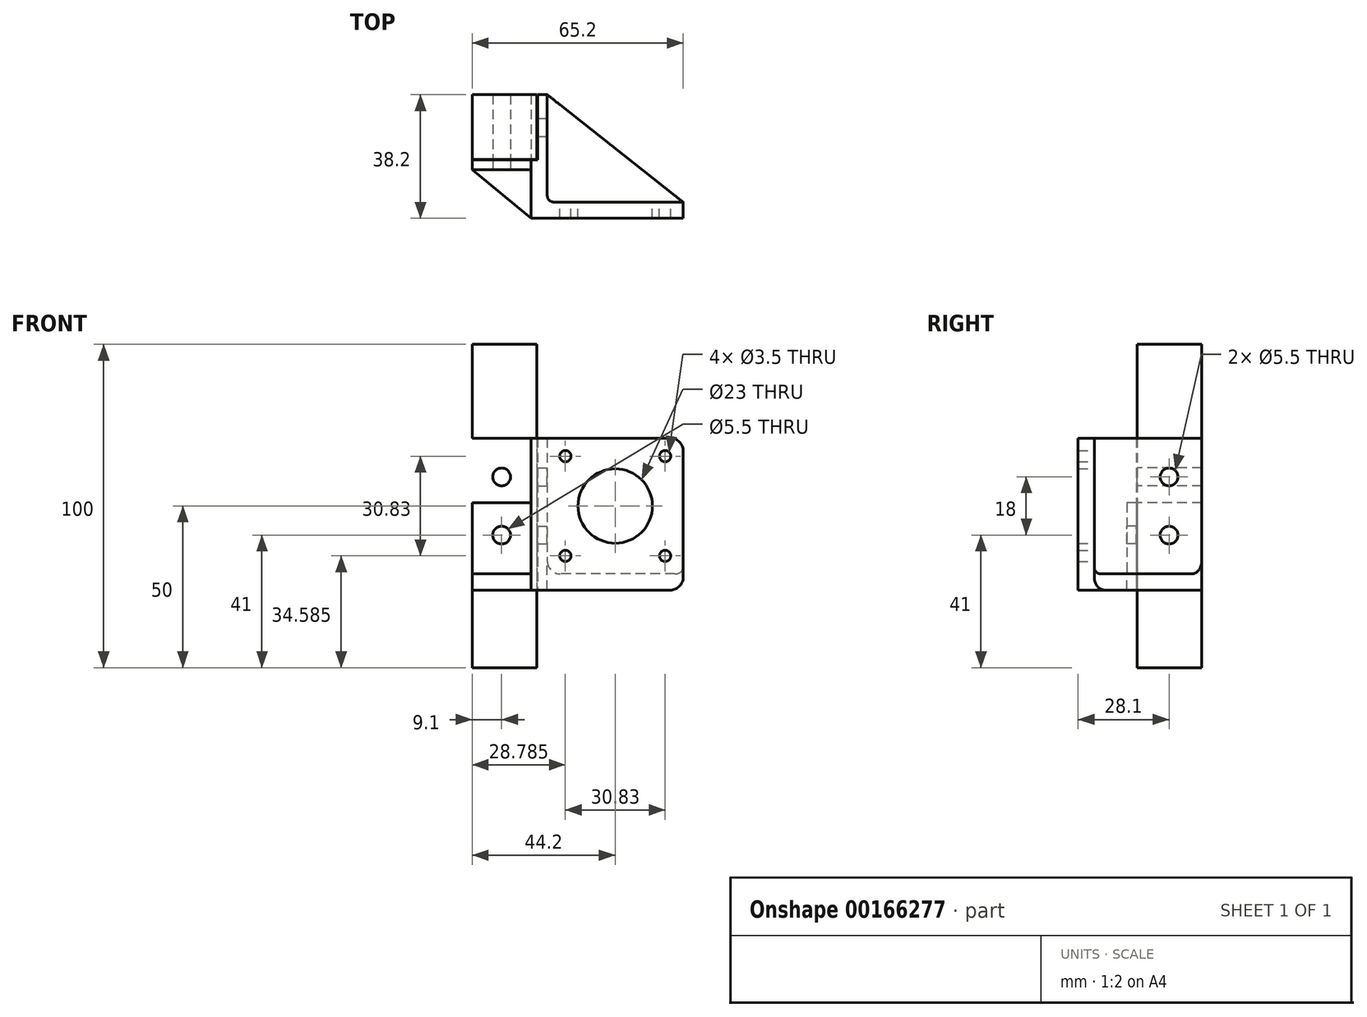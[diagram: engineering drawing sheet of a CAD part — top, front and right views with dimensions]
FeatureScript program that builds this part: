
annotation { "Feature Type Name" : "Feature", "Feature Type Description" : "" }
export const myFeature = defineFeature(function(context is Context, id is Id, definition is map)
    precondition{}
    {
        {
            var Q0;
            Q0=qCreatedBy(makeId("Top.planeOp"),FACE);
            var sketch = newSketch(context, id + "F0", { "sketchPlane" : qUnion([Q0])});
            skLineSegment(sketch, "E0.bottom", {"start": v(10, 10) * mm, "end": v(-10, 10) * mm});
            skLineSegment(sketch, "E0.top", {"start": v(10, -10) * mm, "end": v(-10, -10) * mm});
            skLineSegment(sketch, "E0.left", {"start": v(10, 10) * mm, "end": v(10, -10) * mm});
            skLineSegment(sketch, "E0.right", {"start": v(-10, 10) * mm, "end": v(-10, -10) * mm});
            skPoint(sketch, "E0.middle", {"position": v(0, 0) * mm});
            skSolve(sketch);
        }
        {
            var Q0;
            Q0 = qSketchRegion(id + "F0", true);
            extrude(context, id + "F1", {"entities" : qUnion([Q0]), "endBound" : BoundingType.SYMMETRIC, "depth" : 100 * mm});
        }
        {
            var Q0;
            Q0=qCreatedBy(makeId("Top.planeOp"),FACE);
            var sketch = newSketch(context, id + "F2", { "sketchPlane" : qUnion([Q0])});
            skLineSegment(sketch, "E1.0", {"start": v(10, 10) * mm, "end": v(10, -10) * mm, "construction": true});
            skLineSegment(sketch, "E2.0", {"start": v(10, -10) * mm, "end": v(-10, -10) * mm, "construction": true});
            skLineSegment(sketch, "E3.0", {"start": v(10.2, -10.2) * mm, "end": v(-10, -10.2) * mm});
            skLineSegment(sketch, "E4.0", {"start": v(10.2, 10) * mm, "end": v(10.2, -10.2) * mm});
            skLineSegment(sketch, "E5", {"start": v(10.2, 10) * mm, "end": v(13.2, 10) * mm});
            skLineSegment(sketch, "E6", {"start": v(13.2, 10) * mm, "end": v(13.2, -23.2) * mm});
            skLineSegment(sketch, "E7", {"start": v(-10, -10.2) * mm, "end": v(-10, -13.2) * mm});
            skLineSegment(sketch, "E8", {"start": v(8.2, -28.2) * mm, "end": v(55.2, -28.2) * mm});
            skLineSegment(sketch, "E9", {"start": v(55.2, -28.2) * mm, "end": v(55.2, -23.2) * mm});
            skLineSegment(sketch, "E10", {"start": v(55.2, -23.2) * mm, "end": v(13.2, -23.2) * mm});
            skLineSegment(sketch, "E11", {"start": v(-10, -13.2) * mm, "end": v(8.2, -13.2) * mm});
            skLineSegment(sketch, "E12", {"start": v(8.2, -13.2) * mm, "end": v(8.2, -28.2) * mm});
            skPoint(sketch, "E13.orphan", {"position": v(10.2, -13.2) * mm});
            skSolve(sketch);
        }
        {
            var Q0;
            Q0=makeQuery(id+"F2.imprint","IMPRINT",FACE,{"disambiguationData":[TD([[makeQuery(id+"F2.imprint","IMPRINT",EDGE,{"derivedFrom":sQuery(id+"F2.wireOp",EDGE,"E3.0")}),1.0]])]});
            extrude(context, id + "F3", {"entities" : qUnion([Q0]), "endBound" : BoundingType.SYMMETRIC, "depth" : 42 * mm});
        }
        {
            var Q0;
            Q0=makeQuery(id+"F3.opExtrude","SWEPT_FACE",FACE,{"disambiguationData":[OSD([sQuery(id+"F2.wireOp",EDGE,"E10")])]});
            var sketch = newSketch(context, id + "F4", { "sketchPlane" : qUnion([Q0])});
            skLineSegment(sketch, "E14", {"start": v(-34.2, 21) * mm, "end": v(-34.2, -21) * mm, "construction": true});
            skLineSegment(sketch, "E15", {"start": v(-55.2, 0) * mm, "end": v(-13.2, 0) * mm, "construction": true});
            skLineSegment(sketch, "E16.bottom", {"start": v(-18.79, 15.41) * mm, "end": v(-49.61, 15.41) * mm, "construction": true});
            skLineSegment(sketch, "E16.top", {"start": v(-18.79, -15.41) * mm, "end": v(-49.61, -15.41) * mm, "construction": true});
            skLineSegment(sketch, "E16.left", {"start": v(-18.79, 15.41) * mm, "end": v(-18.79, -15.41) * mm, "construction": true});
            skLineSegment(sketch, "E16.right", {"start": v(-49.61, 15.41) * mm, "end": v(-49.61, -15.41) * mm, "construction": true});
            skPoint(sketch, "E16.middle", {"position": v(-34.2, 0) * mm});
            skCircle(sketch, "E17", {"center": v(-34.2, 0) * mm, "radius": 11.5 * mm});
            skCircle(sketch, "E18", {"center": v(-49.61, 15.41) * mm, "radius": 1.75 * mm});
            skCircle(sketch, "E19.MirrorC", {"center": v(-18.79, 15.41) * mm, "radius": 1.75 * mm});
            skCircle(sketch, "E20.MirrorC", {"center": v(-18.79, -15.41) * mm, "radius": 1.75 * mm});
            skCircle(sketch, "E21.MirrorC", {"center": v(-49.61, -15.41) * mm, "radius": 1.75 * mm});
            skLineSegment(sketch, "E22", {"start": v(-34.2, 0) * mm, "end": v(-55.2, 21) * mm, "construction": true});
            skSolve(sketch);
        }
        {
            var Q0;
            Q0 = qSketchRegion(id + "F4", true);
            extrude(context, id + "F5", {"entities" : qUnion([Q0]), "operationType" : NewBodyOperationType.REMOVE, "endBound" : BoundingType.THROUGH_ALL, "oppositeDirection" : true, "depth" : 25 * mm});
        }
        {
            var Q0;
            Q0=makeQuery(id+"F3.opExtrude","CAP_FACE",FACE,{"disambiguationData":[OSD([sQuery(id+"F2.wireOp",EDGE,"E3.0"),sQuery(id+"F2.wireOp",EDGE,"E4.0"),sQuery(id+"F2.wireOp",EDGE,"E5"),sQuery(id+"F2.wireOp",EDGE,"E6"),sQuery(id+"F2.wireOp",EDGE,"E7"),sQuery(id+"F2.wireOp",EDGE,"E8"),sQuery(id+"F2.wireOp",EDGE,"E9"),sQuery(id+"F2.wireOp",EDGE,"E10"),sQuery(id+"F2.wireOp",EDGE,"E11"),sQuery(id+"F2.wireOp",EDGE,"9BZVBDsl-ltl5-x7Rp-YOd1-Vb26AptN5a61")])],"isStart":true});
            var sketch = newSketch(context, id + "F6", { "sketchPlane" : qUnion([Q0])});
            skLineSegment(sketch, "E23", {"start": v(13.2, -10) * mm, "end": v(55.2, 23.2) * mm});
            skLineSegment(sketch, "E24", {"start": v(55.2, 23.2) * mm, "end": v(55.2, 28.2) * mm});
            skLineSegment(sketch, "E25", {"start": v(55.2, 28.2) * mm, "end": v(8.2, 28.2) * mm});
            skLineSegment(sketch, "E26", {"start": v(8.2, 28.2) * mm, "end": v(-10, 13.2) * mm});
            skLineSegment(sketch, "E27", {"start": v(-10, 13.2) * mm, "end": v(-10, 10.2) * mm});
            skLineSegment(sketch, "E28", {"start": v(-10, 10.2) * mm, "end": v(10.2, 10.2) * mm});
            skLineSegment(sketch, "E29", {"start": v(10.2, 10.2) * mm, "end": v(10.2, -10) * mm});
            skLineSegment(sketch, "E30", {"start": v(10.2, -10) * mm, "end": v(13.2, -10) * mm});
            skSolve(sketch);
        }
        {
            var Q0;
            Q0=makeQuery(id+"F6.imprint","IMPRINT",FACE,{"disambiguationData":[TD([[makeQuery(id+"F6.imprint","IMPRINT",EDGE,{"derivedFrom":sQuery(id+"F6.wireOp",EDGE,"E23")}),1.0]])]});
            var Q1;
            Q1=makeQuery(id+"F6.imprint","IMPRINT",FACE,{"disambiguationData":[TD([[makeQuery(id+"F6.imprint","IMPRINT",EDGE,{"derivedFrom":sQuery(id+"F6.wireOp",EDGE,"E24")}),-1.0]])]});
            var Q2;
            Q2=makeQuery(id+"F6.imprint","IMPRINT",FACE,{"disambiguationData":[TD([[makeQuery(id+"F6.imprint","IMPRINT",EDGE,{"derivedFrom":sQuery(id+"F6.wireOp",EDGE,"E26")}),1.0]])]});
            extrude(context, id + "F7", {"entities" : qUnion([Q0, Q1, Q2]), "operationType" : NewBodyOperationType.ADD, "depth" : 5 * mm});
        }
        {
            var Q0;
            Q0=makeQuery(id+"F3.opExtrude","SWEPT_FACE",FACE,{"disambiguationData":[OSD([sQuery(id+"F2.wireOp",EDGE,"E11")])]});
            var sketch = newSketch(context, id + "F8", { "sketchPlane" : qUnion([Q0])});
            skLineSegment(sketch, "E31", {"start": v(-0.9, 21) * mm, "end": v(-0.9, -21) * mm, "construction": true});
            skCircle(sketch, "E32", {"center": v(-0.9, 9) * mm, "radius": 2.75 * mm});
            skLineSegment(sketch, "E33", {"start": v(-0.9, 0) * mm, "end": v(-10, 0) * mm, "construction": true});
            skCircle(sketch, "E34.MirrorC", {"center": v(-0.9, -9) * mm, "radius": 2.75 * mm});
            skSolve(sketch);
        }
        {
            var Q0;
            Q0 = qSketchRegion(id + "F8", true);
            extrude(context, id + "F9", {"entities" : qUnion([Q0]), "operationType" : NewBodyOperationType.REMOVE, "endBound" : BoundingType.UP_TO_NEXT, "oppositeDirection" : true, "depth" : 25 * mm});
        }
        {
            var Q0;
            Q0=makeQuery(id+"F3.opExtrude","SWEPT_FACE",FACE,{"disambiguationData":[OSD([sQuery(id+"F2.wireOp",EDGE,"E6")])]});
            var sketch = newSketch(context, id + "F10", { "sketchPlane" : qUnion([Q0])});
            skLineSegment(sketch, "E35.0", {"start": v(10, 21) * mm, "end": v(-10.2, 21) * mm, "construction": true});
            skLineSegment(sketch, "E36", {"start": v(-0.1, 21) * mm, "end": v(-0.1, -21) * mm, "construction": true});
            skLineSegment(sketch, "E37", {"start": v(-0.1, 0) * mm, "end": v(10, 0) * mm, "construction": true});
            skCircle(sketch, "E38", {"center": v(-0.1, 9) * mm, "radius": 2.75 * mm});
            skCircle(sketch, "E39.MirrorC", {"center": v(-0.1, -9) * mm, "radius": 2.75 * mm});
            skSolve(sketch);
        }
        {
            var Q0;
            Q0 = qSketchRegion(id + "F10", true);
            extrude(context, id + "F11", {"entities" : qUnion([Q0]), "operationType" : NewBodyOperationType.REMOVE, "endBound" : BoundingType.UP_TO_NEXT, "oppositeDirection" : true, "depth" : 25 * mm});
        }
        {
            var Q0;
            Q0=makeQuery(id+"F3.opExtrude","CAP_EDGE",EDGE,{"disambiguationData":[OSD([sQuery(id+"F2.wireOp",EDGE,"E6")])],"isStart":true});
            var Q1;
            Q1=makeQuery(id+"F3.opExtrude","CAP_EDGE",EDGE,{"disambiguationData":[OSD([sQuery(id+"F2.wireOp",EDGE,"E11")])],"isStart":true});
            var Q2;
            Q2=makeQuery(id+"F3.opExtrude","CAP_EDGE",EDGE,{"disambiguationData":[OSD([sQuery(id+"F2.wireOp",EDGE,"E9")])],"isStart":false});
            var Q3;
            Q3=makeQuery(id+"F7.opExtrude","CAP_EDGE",EDGE,{"disambiguationData":[OSD([sQuery(id+"F6.wireOp",EDGE,"E24")])],"isStart":false});
            fillet(context, id + "F12", {"entities" : qUnion([Q0, Q1, Q2, Q3]), "radius" : 4 * mm, "tangentPropagation" : true, "allowEdgeOverflow" : false});
        }
        {
            var Q0;
            Q0=makeQuery(id+"F3.opExtrude","CAP_EDGE",EDGE,{"disambiguationData":[OSD([sQuery(id+"F2.wireOp",EDGE,"E10")])],"isStart":true});
            fillet(context, id + "F13", {"entities" : qUnion([Q0]), "radius" : 2 * mm, "tangentPropagation" : true, "allowEdgeOverflow" : false});
        }
        {
            var Q0;
            Q0=makeQuery(id+"F3.opExtrude","SWEPT_FACE",FACE,{"disambiguationData":[OSD([sQuery(id+"F2.wireOp",EDGE,"E11")])]});
            var sketch = newSketch(context, id + "F14", { "sketchPlane" : qUnion([Q0])});
            skLineSegment(sketch, "E40.bottom", {"start": v(8.2, 21) * mm, "end": v(-10, 21) * mm});
            skLineSegment(sketch, "E40.top", {"start": v(8.2, 1) * mm, "end": v(-10, 1) * mm});
            skLineSegment(sketch, "E40.left", {"start": v(8.2, 21) * mm, "end": v(8.2, 1) * mm});
            skLineSegment(sketch, "E40.right", {"start": v(-10, 21) * mm, "end": v(-10, 1) * mm});
            skSolve(sketch);
        }
        {
            var Q0;
            Q0=makeQuery(id+"F14.imprint","IMPRINT",FACE,{"disambiguationData":[TD([[makeQuery(id+"F14.imprint","IMPRINT",EDGE,{"derivedFrom":sQuery(id+"F14.wireOp",EDGE,"BBVPBk5C-NKpx-Xrrf-ylvQ-LpUPS9nrs2PJ.top")}),-1.0]])]});
            var Q1;
            Q1=makeQuery(id+"F14.imprint","IMPRINT",FACE,{"disambiguationData":[TD([[makeQuery(id+"F14.imprint","IMPRINT",EDGE,{"derivedFrom":sQuery(id+"F14.wireOp",EDGE,"E40.bottom")}),-1.0]])]});
            extrude(context, id + "F15", {"entities" : qUnion([Q0, Q1]), "operationType" : NewBodyOperationType.REMOVE, "oppositeDirection" : true, "depth" : 25 * mm});
        }
    });
